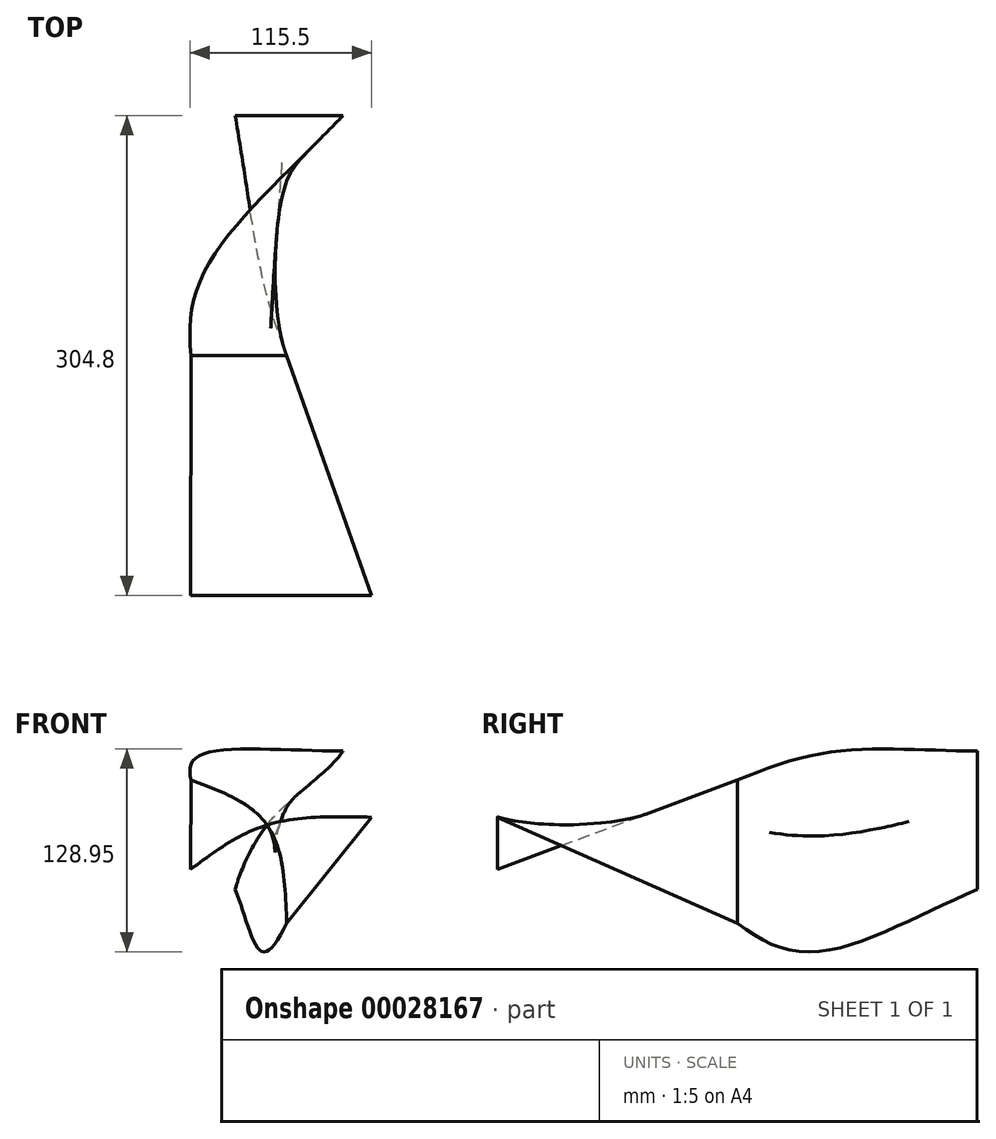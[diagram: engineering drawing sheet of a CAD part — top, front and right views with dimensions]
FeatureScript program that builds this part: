
annotation { "Feature Type Name" : "Feature", "Feature Type Description" : "" }
export const myFeature = defineFeature(function(context is Context, id is Id, definition is map)
    precondition{}
    {
        {
            var Q0;
            Q0=qCreatedBy(makeId("Front.planeOp"),FACE);
            cPlane(context, id + "F0", {"entities" : qUnion([Q0]), "cplaneType" : CPlaneType.OFFSET, "offset" : 152.4 * mm, "width" : 152.4 * mm, "height" : 152.4 * mm});
        }
        {
            var Q0;
            Q0=qCreatedBy(makeId("Front.planeOp"),FACE);
            cPlane(context, id + "F1", {"entities" : qUnion([Q0]), "cplaneType" : CPlaneType.OFFSET, "offset" : 152.4 * mm, "oppositeDirection" : true, "width" : 152.4 * mm, "height" : 152.4 * mm});
        }
        {
            var Q0;
            Q0=qCreatedBy(makeId("Front.planeOp"),FACE);
            var sketch = newSketch(context, id + "F2", { "sketchPlane" : qUnion([Q0])});
            skFitSpline(sketch, "E0", {"points": [v(-48.4, 28.65) * mm, v(0, 0) * mm, v(12.4, -62.6) * mm], "startDerivative": vector(118.34, -44.1) * mm, "endDerivative": vector(4.44, -137.43) * mm});
            skSolve(sketch);
        }
        {
            var Q0;
            Q0=qCreatedBy(id+"F0.planeOp",FACE);
            var sketch = newSketch(context, id + "F3", { "sketchPlane" : qUnion([Q0])});
            skFitSpline(sketch, "E1", {"points": [v(-48.67, -28.23) * mm, v(0, 0) * mm, v(66.43, 4.89) * mm], "startDerivative": vector(95.44, 70.8) * mm, "endDerivative": vector(134.22, -3.53) * mm});
            skSolve(sketch);
        }
        {
            var Q0;
            Q0=qCreatedBy(id+"F1.planeOp",FACE);
            var sketch = newSketch(context, id + "F4", { "sketchPlane" : qUnion([Q0])});
            skFitSpline(sketch, "E2", {"points": [v(-20.3, -40.86) * mm, v(0, 0) * mm, v(35.51, 33.13) * mm, v(48.26, 46.9) * mm], "startDerivative": vector(24.39, 87.22) * mm, "endDerivative": vector(18.92, 29.32) * mm});
            skSolve(sketch);
        }
        {
            var Q0;
            Q0=sQuery(id+"F3.wireOp",EDGE,"E1");
            var Q1;
            Q1=sQuery(id+"F2.wireOp",EDGE,"E0");
            loft(context, id + "F5", {"bodyType" : ToolBodyType.SURFACE, "wireProfilesArray" : [{ "wireProfileEntities" : qUnion([Q0]) }, { "wireProfileEntities" : qUnion([Q1]) }]});
        }
        {
            var Q0;
            Q0=makeQuery(id+"F5.opLoft","MID_CAP_EDGE",EDGE,{"disambiguationData":[OSD([sQuery(id+"F2.wireOp",VERTEX,"E0.start"),sQuery(id+"F2.wireOp",VERTEX,"E0.end"),sQuery(id+"F2.wireOp",EDGE,"E0")])],"capPos":1.0});
            var Q1;
            Q1=sQuery(id+"F4.wireOp",EDGE,"E2");
            loft(context, id + "F6", {"bodyType" : ToolBodyType.SURFACE, "startCondition" : LoftEndDerivativeType.MATCH_CURVATURE, "startMagnitude" : 1, "wireProfilesArray" : [{ "wireProfileEntities" : qUnion([Q0]) }, { "wireProfileEntities" : qUnion([Q1]) }]});
        }
    });
